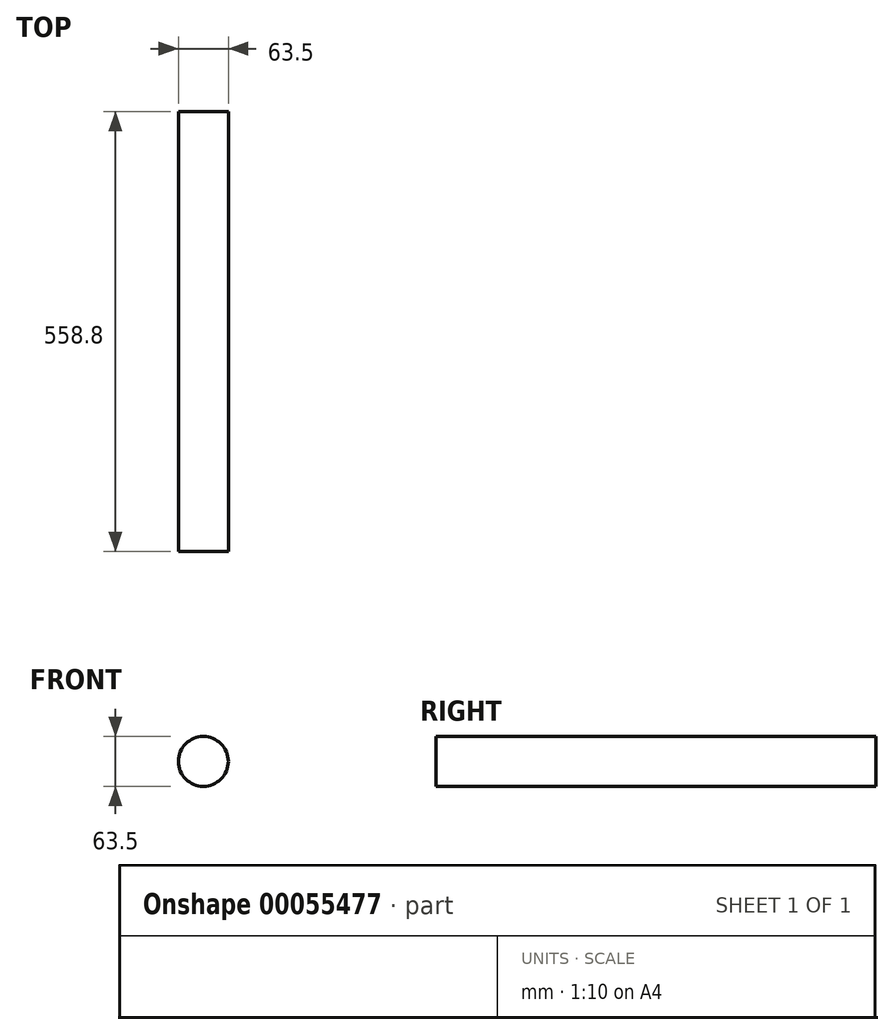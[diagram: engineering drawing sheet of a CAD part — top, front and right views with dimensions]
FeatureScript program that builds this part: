
annotation { "Feature Type Name" : "Feature", "Feature Type Description" : "" }
export const myFeature = defineFeature(function(context is Context, id is Id, definition is map)
    precondition{}
    {
        {
            var Q0;
            Q0=qCreatedBy(makeId("Front.planeOp"),FACE);
            var sketch = newSketch(context, id + "F0", { "sketchPlane" : qUnion([Q0])});
            skCircle(sketch, "E0", {"center": v(0, 0) * mm, "radius": 31.75 * mm});
            skSolve(sketch);
        }
        {
            var Q0;
            Q0=makeQuery(id+"F0.imprint","IMPRINT",FACE,{"disambiguationData":[TD([[makeQuery(id+"F0.imprint","IMPRINT",EDGE,{"derivedFrom":sQuery(id+"F0.wireOp",EDGE,"E0")}),1.0]])]});
            extrude(context, id + "F1", {"entities" : qUnion([Q0]), "depth" : 558.8 * mm});
        }
    });
